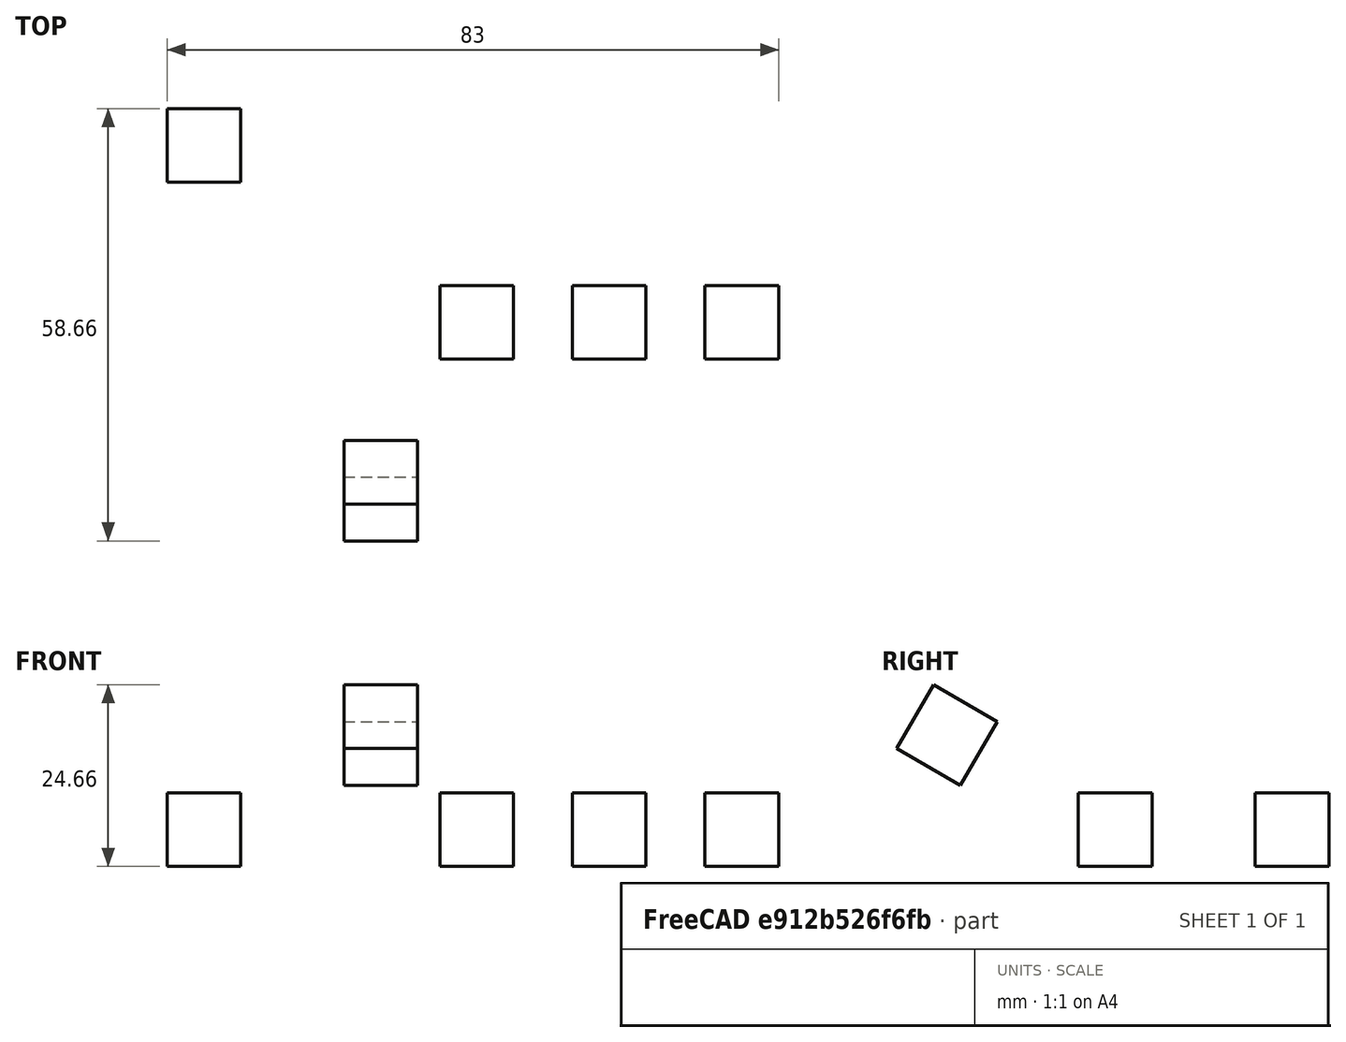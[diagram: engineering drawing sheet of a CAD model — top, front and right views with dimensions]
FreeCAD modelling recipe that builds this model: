
FCSTD DOCUMENT  (FreeCAD 0.18.1R)
Label: sub1_1_1
License: All rights reserved
LicenseURL: http://en.wikipedia.org/wiki/All_rights_reserved
objects: Part::Box×5
note: 5 computed .brp shape members not serialized (recipe doc carries the construction recipe); baked Part::Feature solids carry a one-line shape summary decoded from their .brp

FEATURE [Part::Box] Box  label="Cube"
  AttacherType = Attacher::AttachEngine3D
  Height = 10
  Length = 10
  Placement = pos=(-37,24,0) rot=(0,0,1;0rad)
  Width = 10
FEATURE [Part::Box] Box001  label="Cube001"
  AttacherType = Attacher::AttachEngine3D
  Height = 10
  Length = 10
  Placement = pos=(18,0,0) rot=(0,0,1;0rad)
  Width = 10
FEATURE [Part::Box] Box002  label="Cube002"
  AttacherType = Attacher::AttachEngine3D
  Height = 10
  Length = 10
  Placement = pos=(36,0,0) rot=(0,0,1;0rad)
  Width = 10
FEATURE [Part::Box] Box003  label="Cube003"
  AttacherType = Attacher::AttachEngine3D
  Height = 10
  Length = 10
  Placement = pos=(-13,-16,11) rot=(1,0,0;1.0472rad)
  Width = 10
FEATURE [Part::Box] Box004  label="Cube004"
  AttacherType = Attacher::AttachEngine3D
  Height = 10
  Length = 10
  Width = 10
